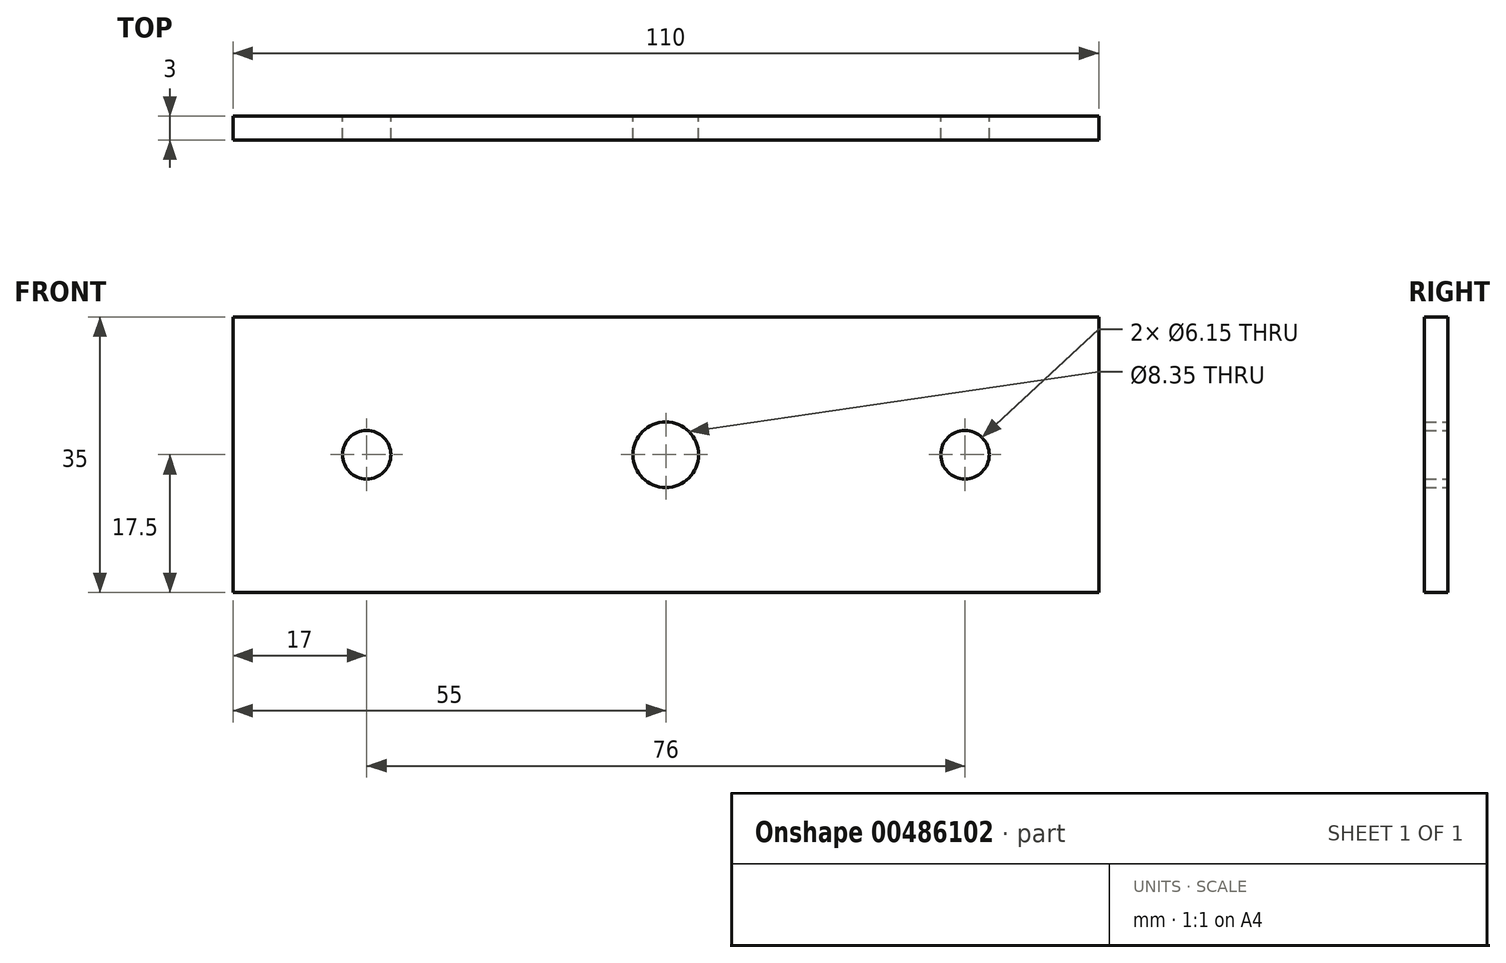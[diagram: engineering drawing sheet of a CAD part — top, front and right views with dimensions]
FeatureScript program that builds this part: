
annotation { "Feature Type Name" : "Feature", "Feature Type Description" : "" }
export const myFeature = defineFeature(function(context is Context, id is Id, definition is map)
    precondition{}
    {
        {
            var Q0;
            Q0=qCreatedBy(makeId("Front.planeOp"),FACE);
            var sketch = newSketch(context, id + "F0", { "sketchPlane" : qUnion([Q0])});
            skLineSegment(sketch, "E0.bottom", {"start": v(55, 17.5) * mm, "end": v(-55, 17.5) * mm});
            skLineSegment(sketch, "E0.top", {"start": v(55, -17.5) * mm, "end": v(-55, -17.5) * mm});
            skLineSegment(sketch, "E0.left", {"start": v(55, 17.5) * mm, "end": v(55, -17.5) * mm});
            skLineSegment(sketch, "E0.right", {"start": v(-55, 17.5) * mm, "end": v(-55, -17.5) * mm});
            skPoint(sketch, "E0.middle", {"position": v(0, 0) * mm});
            skCircle(sketch, "E1", {"center": v(0, 0) * mm, "radius": 4.17 * mm});
            skCircle(sketch, "E2", {"center": v(-38, 0) * mm, "radius": 3.07 * mm});
            skCircle(sketch, "E3", {"center": v(38, 0) * mm, "radius": 3.08 * mm});
            skSolve(sketch);
        }
        {
            var Q0;
            Q0=makeQuery(id+"F0.imprint","IMPRINT",FACE,{"disambiguationData":[TD([[makeQuery(id+"F0.imprint","IMPRINT",EDGE,{"derivedFrom":sQuery(id+"F0.wireOp",EDGE,"E0.bottom")}),1.0]])]});
            extrude(context, id + "F1", {"entities" : qUnion([Q0]), "depth" : 3 * mm});
        }
    });
